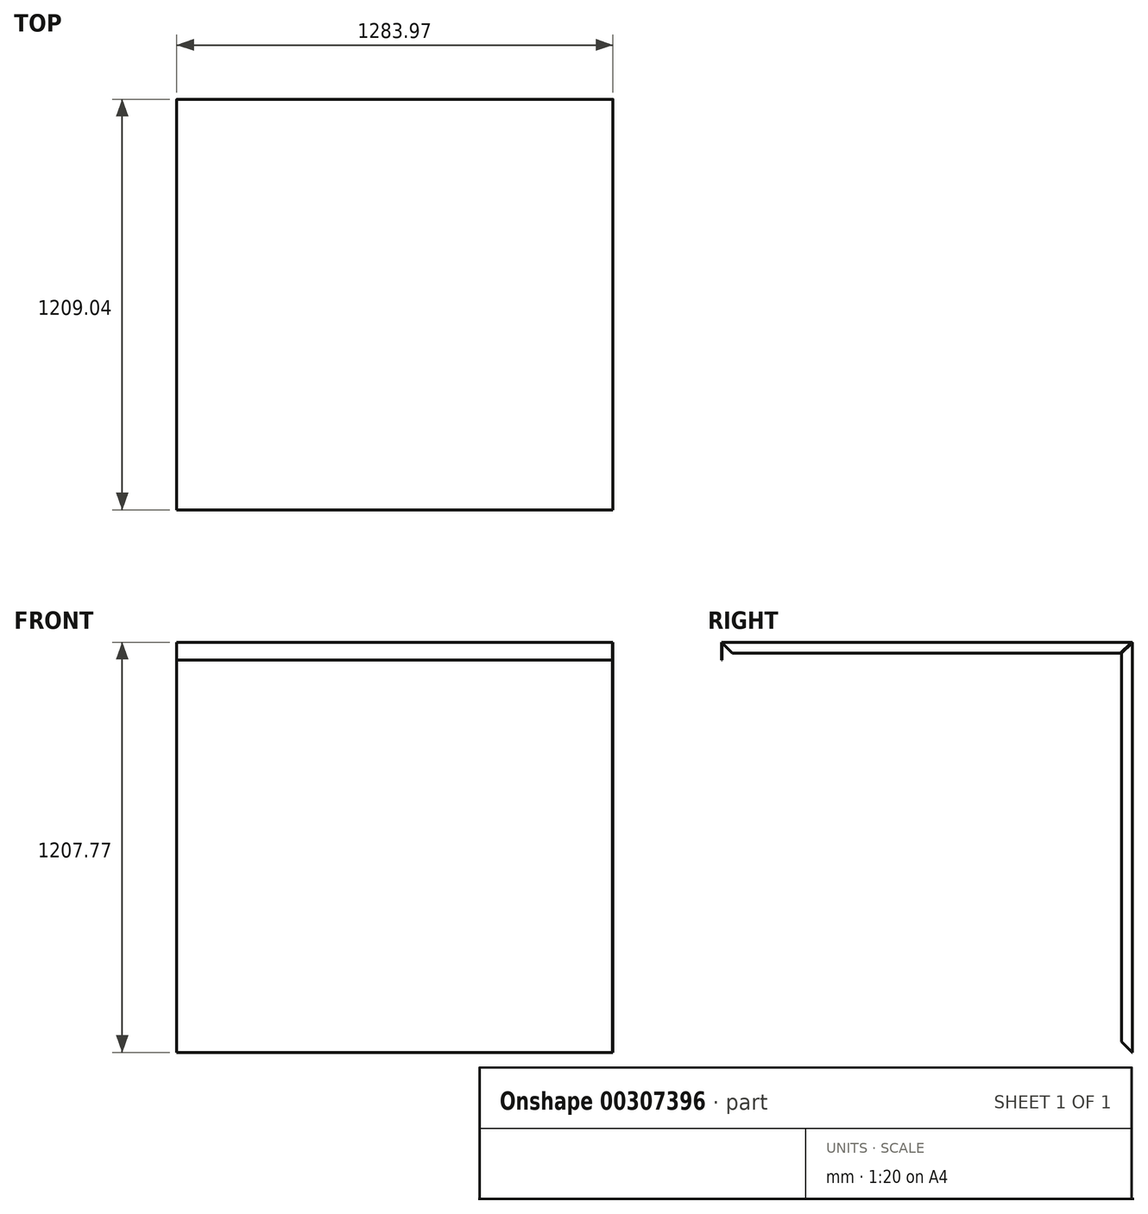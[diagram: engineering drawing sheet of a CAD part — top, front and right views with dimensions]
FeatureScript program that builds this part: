
annotation { "Feature Type Name" : "Feature", "Feature Type Description" : "" }
export const myFeature = defineFeature(function(context is Context, id is Id, definition is map)
    precondition{}
    {
        {
            var Q0;
            Q0=qCreatedBy(makeId("Right.planeOp"),FACE);
            var sketch = newSketch(context, id + "F0", { "sketchPlane" : qUnion([Q0])});
            skLineSegment(sketch, "E0", {"start": v(0, 0) * mm, "end": v(-1.27, 0) * mm});
            skLineSegment(sketch, "E1", {"start": v(-1.27, 0) * mm, "end": v(-1.27, 52.07) * mm});
            skLineSegment(sketch, "E2", {"start": v(-1.27, 52.07) * mm, "end": v(1207.77, 52.07) * mm});
            skLineSegment(sketch, "E3", {"start": v(1207.77, 52.07) * mm, "end": v(1207.77, -1155.7) * mm});
            skLineSegment(sketch, "E4", {"start": v(0, 0) * mm, "end": v(0, 50.8) * mm});
            skLineSegment(sketch, "E5", {"start": v(0, 50.8) * mm, "end": v(1206.5, 50.8) * mm});
            skLineSegment(sketch, "E6", {"start": v(1206.5, 50.8) * mm, "end": v(1206.5, -1155.7) * mm});
            skLineSegment(sketch, "E7", {"start": v(1206.5, -1155.7) * mm, "end": v(1207.77, -1155.7) * mm});
            skLineSegment(sketch, "E8", {"start": v(1206.5, 50.8) * mm, "end": v(1206.5, 52.07) * mm, "construction": true});
            skSolve(sketch);
        }
        {
            var Q0;
            Q0 = qSketchRegion(id + "F0", true);
            extrude(context, id + "F1", {"entities" : qUnion([Q0]), "endBound" : BoundingType.SYMMETRIC, "depth" : 1282.7 * mm});
        }
        {
            var Q0;
            Q0=makeQuery(id+"F1.opExtrude","SWEPT_EDGE",EDGE,{"disambiguationData":[OSD([sQuery(id+"F0.wireOp",EDGE,"E2"),sQuery(id+"F0.wireOp",EDGE,"E3")])]});
            fillet(context, id + "F2", {"entities" : qUnion([Q0]), "radius" : 2.54 * mm, "tangentPropagation" : true, "allowEdgeOverflow" : false});
        }
        {
            var Q0;
            Q0=makeQuery(id+"F1.opExtrude","CAP_FACE",FACE,{"disambiguationData":[OSD([sQuery(id+"F0.wireOp",EDGE,"E0"),sQuery(id+"F0.wireOp",EDGE,"E1"),sQuery(id+"F0.wireOp",EDGE,"E2"),sQuery(id+"F0.wireOp",EDGE,"E3"),sQuery(id+"F0.wireOp",EDGE,"E4"),sQuery(id+"F0.wireOp",EDGE,"E5"),sQuery(id+"F0.wireOp",EDGE,"E6"),sQuery(id+"F0.wireOp",EDGE,"E7")])],"isStart":false});
            var sketch = newSketch(context, id + "F3", { "sketchPlane" : qUnion([Q0])});
            skLineSegment(sketch, "E9", {"start": v(-1.27, 52.07) * mm, "end": v(30.48, 20.32) * mm});
            skLineSegment(sketch, "E10.1", {"start": v(-1.27, 52.07) * mm, "end": v(1205.23, 52.07) * mm});
            skLineSegment(sketch, "E11", {"start": v(-1.27, 0) * mm, "end": v(-1.27, 52.07) * mm, "construction": true});
            skArc(sketch, "E12.0", {"start": v(1207.77, 49.53) * mm, "mid": v(1207.03, 51.33) * mm, "end": v(1205.23, 52.07) * mm});
            skPoint(sketch, "E13", {"position": v(17.78, 33.02) * mm});
            skLineSegment(sketch, "E14", {"start": v(30.48, 20.32) * mm, "end": v(1172.27, 20.32) * mm});
            skLineSegment(sketch, "E15", {"start": v(1172.27, 20.32) * mm, "end": v(1204.25, 50.8) * mm});
            skLineSegment(sketch, "E16", {"start": v(1204.25, 50.8) * mm, "end": v(1206.5, 50.8) * mm});
            skLineSegment(sketch, "E17", {"start": v(1206.5, 50.8) * mm, "end": v(1206.5, 48.55) * mm});
            skLineSegment(sketch, "E18", {"start": v(1206.5, 48.55) * mm, "end": v(1176.02, 19.5) * mm});
            skLineSegment(sketch, "E19", {"start": v(1176.02, 19.5) * mm, "end": v(1176.02, -1123.95) * mm});
            skLineSegment(sketch, "E20", {"start": v(1207.77, 49.53) * mm, "end": v(1207.77, -1155.7) * mm});
            skLineSegment(sketch, "E21", {"start": v(1207.77, -1155.7) * mm, "end": v(1176.02, -1123.95) * mm});
            skLineSegment(sketch, "E22", {"start": v(1176.02, -1123.95) * mm, "end": v(1207.77, -1123.95) * mm, "construction": true});
            skLineSegment(sketch, "E23", {"start": v(30.48, 20.32) * mm, "end": v(30.48, 52.07) * mm, "construction": true});
            skLineSegment(sketch, "E24", {"start": v(1207.77, -1155.7) * mm, "end": v(1207.77, -1123.95) * mm});
            skSolve(sketch);
        }
        {
            var Q0;
            Q0 = qSketchRegion(id + "F3", true);
            extrude(context, id + "F4", {"entities" : qUnion([Q0]), "operationType" : NewBodyOperationType.ADD, "depth" : 1.27 * mm});
        }
    });
